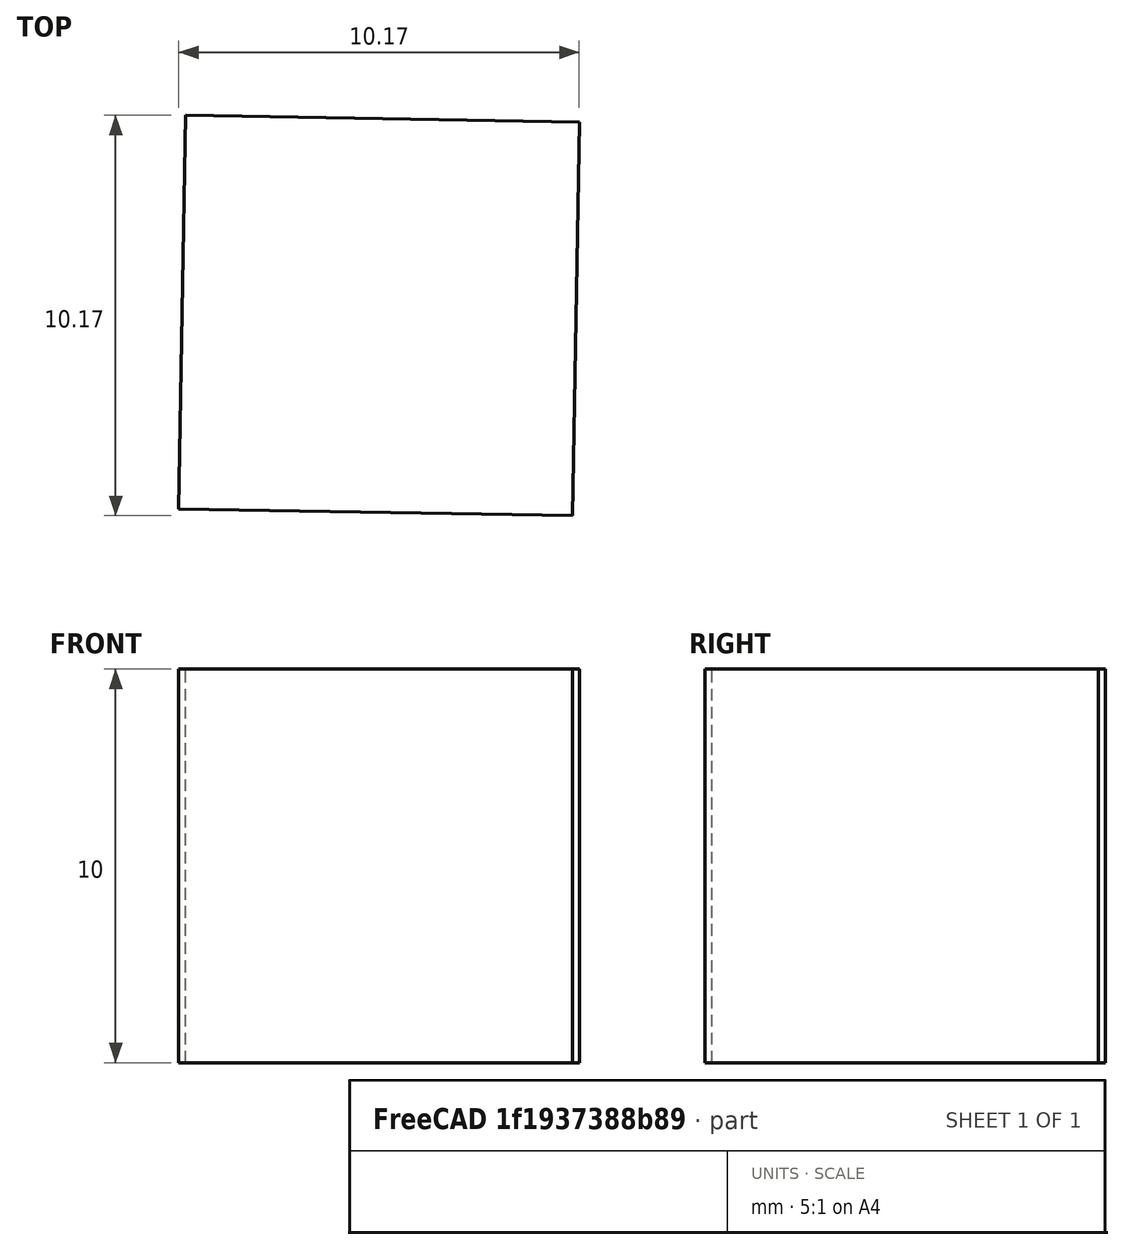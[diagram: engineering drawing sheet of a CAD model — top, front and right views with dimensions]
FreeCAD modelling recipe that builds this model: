
FCSTD DOCUMENT  (FreeCAD 0.21R33694 (Git))
Label: OJT1_T11P01_
License: All rights reserved
LicenseURL: http://en.wikipedia.org/wiki/All_rights_reserved
objects: Part::Box×1, Part::FeaturePython×1
note: 1 computed .brp shape members not serialized (recipe doc carries the construction recipe); baked Part::Feature solids carry a one-line shape summary decoded from their .brp

FEATURE [Part::Box] Box  label="Cube"
  AttacherType = Attacher::AttachEngine3D
  Height = 10
  Length = 10
  Placement = pos=(20,-5,0) rot=(0,0,-1;0.017453rad)
  Width = 10
FEATURE [Part::FeaturePython] Array  # Draft array (typed FeaturePython)
  AlwaysSyncPlacement = false
  Angle = 180
  ArrayType = 1
  Axis = (0,0,1)
  Base = -> Box
  Center = (0,0,0)
  Count = 6
  ExpandArray = false
  Fuse = false
  IntervalAxis = (0,0,0)
  IntervalX = (100,0,0)
  IntervalY = (0,100,0)
  IntervalZ = (0,0,100)
  NumberCircles = 3
  NumberPolar = 6
  NumberX = 2
  NumberY = 2
  NumberZ = 1
  PlacementList = 6 placements: [(20,-5,0),(19.1193,7.71062,0),(10.9356,17.476,0),(-1.42506,20.5662,0),(-13.2414,15.8008,0),(-20,5,0)]
  RadialDistance = 50
  ScaleList = (6) [(1,1,1),(1,1,1),(1,1,1),(1,1,1),(1,1,1),(1,1,1)]
  Symmetry = 1
  TangentialDistance = 25
